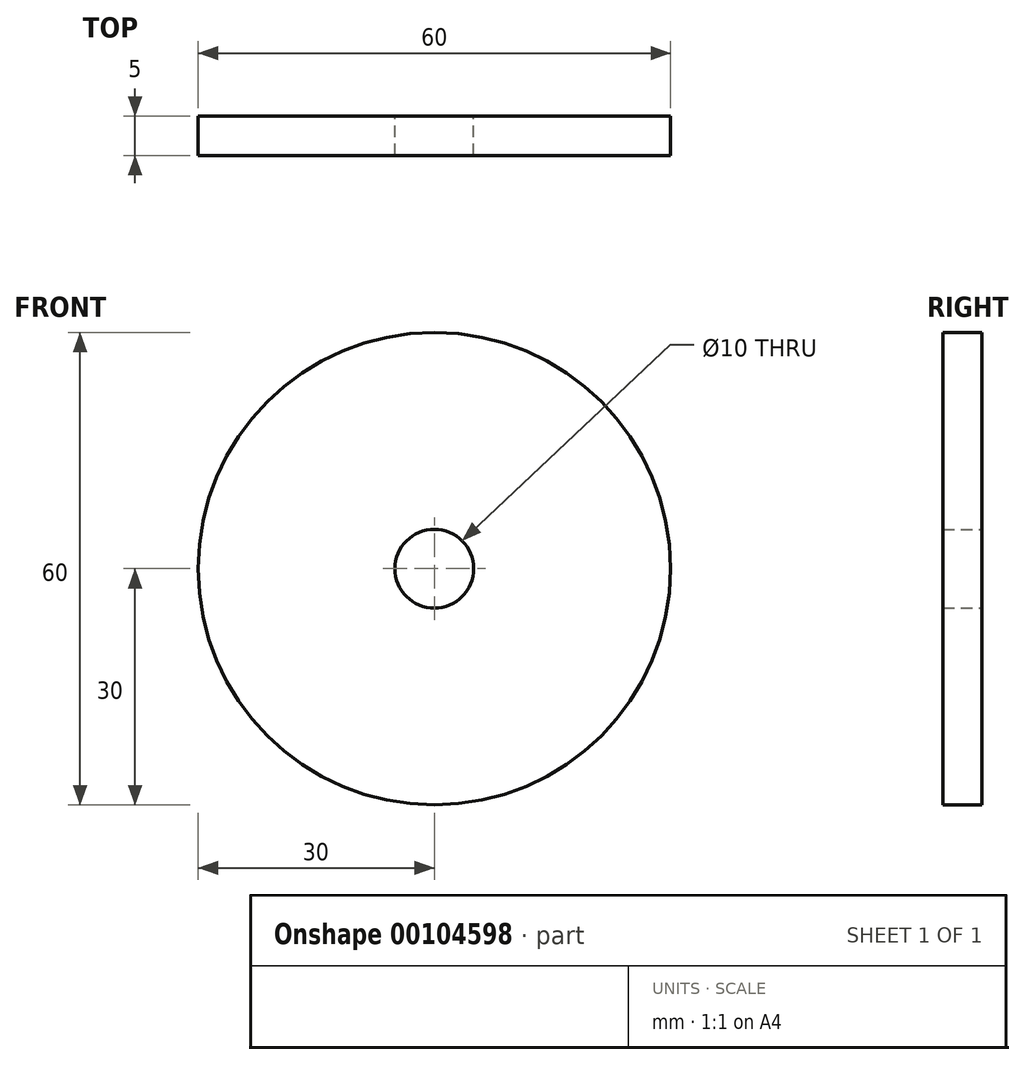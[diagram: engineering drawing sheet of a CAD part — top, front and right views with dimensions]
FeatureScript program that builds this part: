
annotation { "Feature Type Name" : "Feature", "Feature Type Description" : "" }
export const myFeature = defineFeature(function(context is Context, id is Id, definition is map)
    precondition{}
    {
        {
            var Q0;
            Q0=qCreatedBy(makeId("Front.planeOp"),FACE);
            var sketch = newSketch(context, id + "F0", { "sketchPlane" : qUnion([Q0])});
            skCircle(sketch, "E0", {"center": v(0, 0) * mm, "radius": 30 * mm});
            skCircle(sketch, "E1", {"center": v(0, 0) * mm, "radius": 5 * mm});
            skSolve(sketch);
        }
        {
            var Q0;
            Q0 = qSketchRegion(id + "F0", true);
            var Q1;
            Q1=makeQuery(id+"F0.imprint","IMPRINT",FACE,{"disambiguationData":[TD([[makeQuery(id+"F0.imprint","IMPRINT",EDGE,{"derivedFrom":sQuery(id+"F0.wireOp",EDGE,"E0")}),1.0]])]});
            extrude(context, id + "F1", {"entities" : qUnion([Q0, Q1]), "depth" : 5 * mm});
        }
    });
